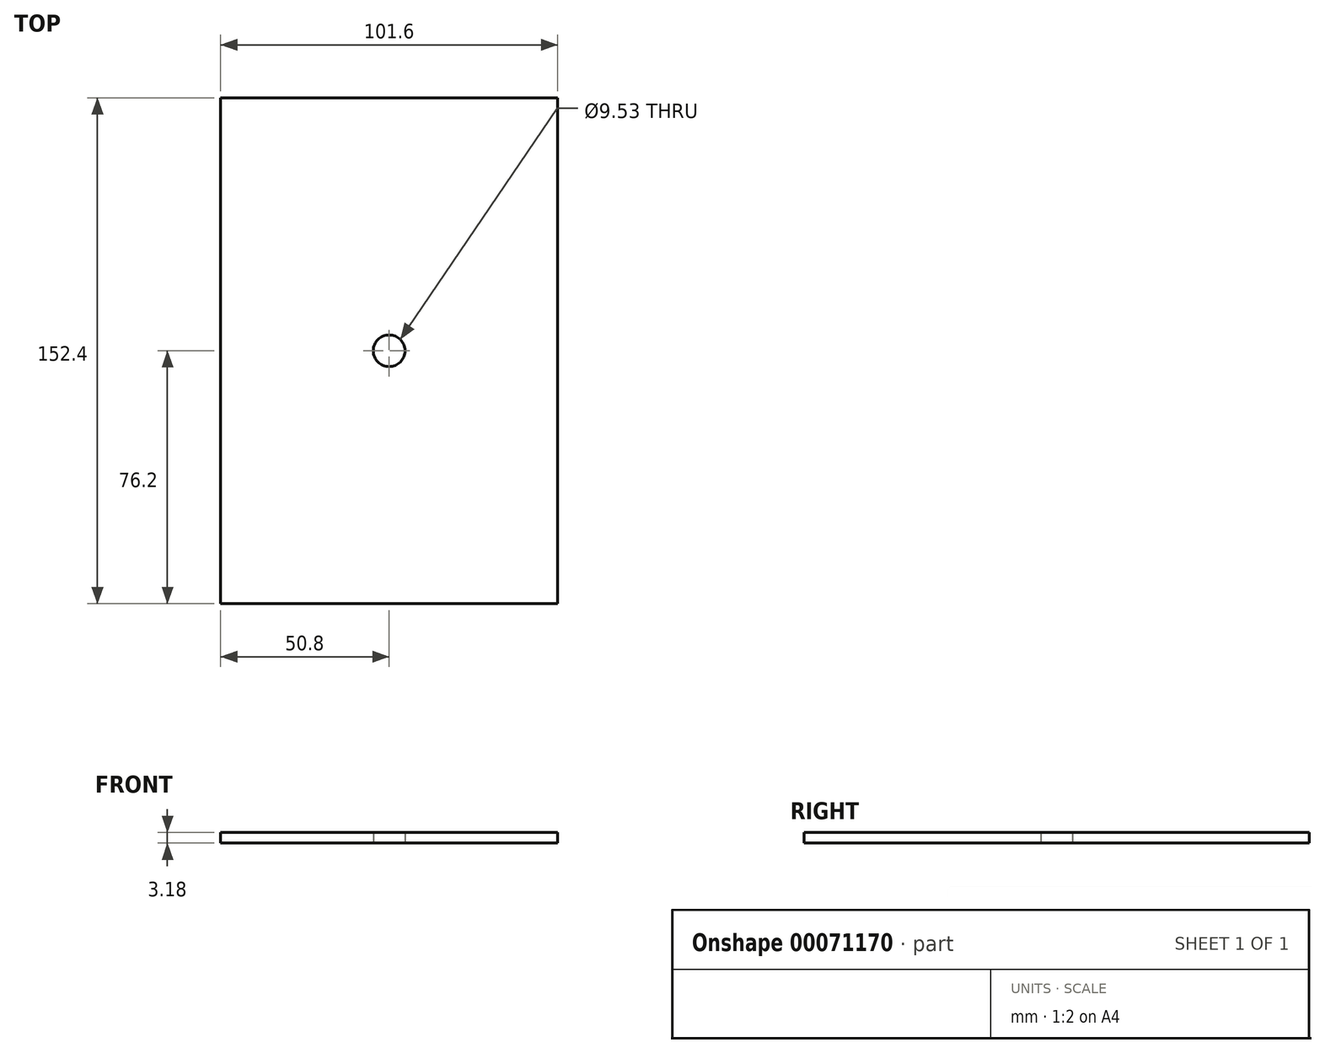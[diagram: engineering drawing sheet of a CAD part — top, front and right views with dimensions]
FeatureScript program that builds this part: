
annotation { "Feature Type Name" : "Feature", "Feature Type Description" : "" }
export const myFeature = defineFeature(function(context is Context, id is Id, definition is map)
    precondition{}
    {
        {
            var Q0;
            Q0=qCreatedBy(makeId("Top.planeOp"),FACE);
            var sketch = newSketch(context, id + "F0", { "sketchPlane" : qUnion([Q0])});
            skLineSegment(sketch, "E0.rect.bottom", {"start": v(50.8, 76.2) * mm, "end": v(-50.8, 76.2) * mm});
            skLineSegment(sketch, "E0.rect.top", {"start": v(50.8, -76.2) * mm, "end": v(-50.8, -76.2) * mm});
            skLineSegment(sketch, "E0.rect.left", {"start": v(50.8, 76.2) * mm, "end": v(50.8, -76.2) * mm});
            skLineSegment(sketch, "E0.rect.right", {"start": v(-50.8, 76.2) * mm, "end": v(-50.8, -76.2) * mm});
            skPoint(sketch, "E0.rect.middle", {"position": v(0, 0) * mm});
            skCircle(sketch, "E1", {"center": v(0, 0) * mm, "radius": 4.76 * mm});
            skSolve(sketch);
        }
        {
            var Q0;
            Q0=makeQuery(id+"F0.imprint","IMPRINT",FACE,{"disambiguationData":[TD([[makeQuery(id+"F0.imprint","IMPRINT",EDGE,{"derivedFrom":sQuery(id+"F0.wireOp",EDGE,"E0.rect.bottom")}),1.0]])]});
            extrude(context, id + "F1", {"entities" : qUnion([Q0]), "depth" : 3.17 * mm});
        }
    });
